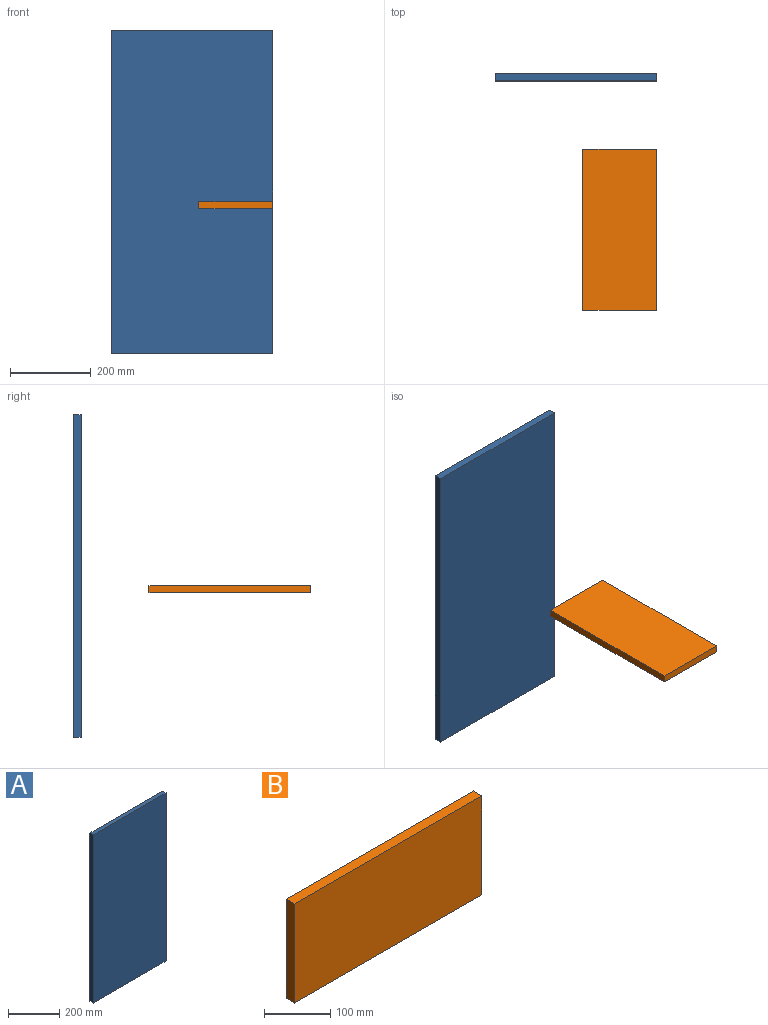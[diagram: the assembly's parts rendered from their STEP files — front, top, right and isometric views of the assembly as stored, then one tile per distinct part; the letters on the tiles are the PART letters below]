
ASSEMBLY  parts=2 mates=1
PART A: 6 faces, bbox 400x18x800 mm
  f0: plane 800x18mm, normal (-1,0,0), area 14400mm2, adj f1,f3,f4,f5
  f1: plane 400x18mm, normal (0,0,-1), area 7200mm2, adj f0,f2,f4,f5
  f2: plane 800x18mm, normal (1,0,0), area 14400mm2, adj f1,f3,f4,f5
  f3: plane 400x18mm, normal (0,0,1), area 7200mm2, adj f0,f2,f4,f5
  f4: plane 800x400mm, normal (0,-1,0), area 320000mm2, adj f0,f1,f2,f3
  f5: plane 800x400mm, normal (0,1,0), area 320000mm2, adj f0,f1,f2,f3
PART B: 6 faces, bbox 400x18x183 mm
  f0: plane 183.03x18mm, normal (-1,0,0), area 3294.6mm2, adj f1,f3,f4,f5
  f1: plane 400x18mm, normal (0,0,-1), area 7200mm2, adj f0,f2,f4,f5
  f2: plane 183.03x18mm, normal (1,0,0), area 3294.6mm2, adj f1,f3,f4,f5
  f3: plane 400x18mm, normal (0,0,1), area 7200mm2, adj f0,f2,f4,f5
  f4: plane 400x183.03mm, normal (0,-1,0), area 73213.3mm2, adj f0,f1,f2,f3
  f5: plane 400x183.03mm, normal (0,1,0), area 73213.3mm2, adj f0,f1,f2,f3
PLACE A t=(-345.81,-352.26,-93.74)mm
PLACE B rot(axis=(-0.58,-0.58,0.58),120deg) t=(54.19,-938.85,264.48)mm
MATE planar B.f1 <-> A.f2  axis (1,0,0) through (54.19,-738.85,273.48)mm
